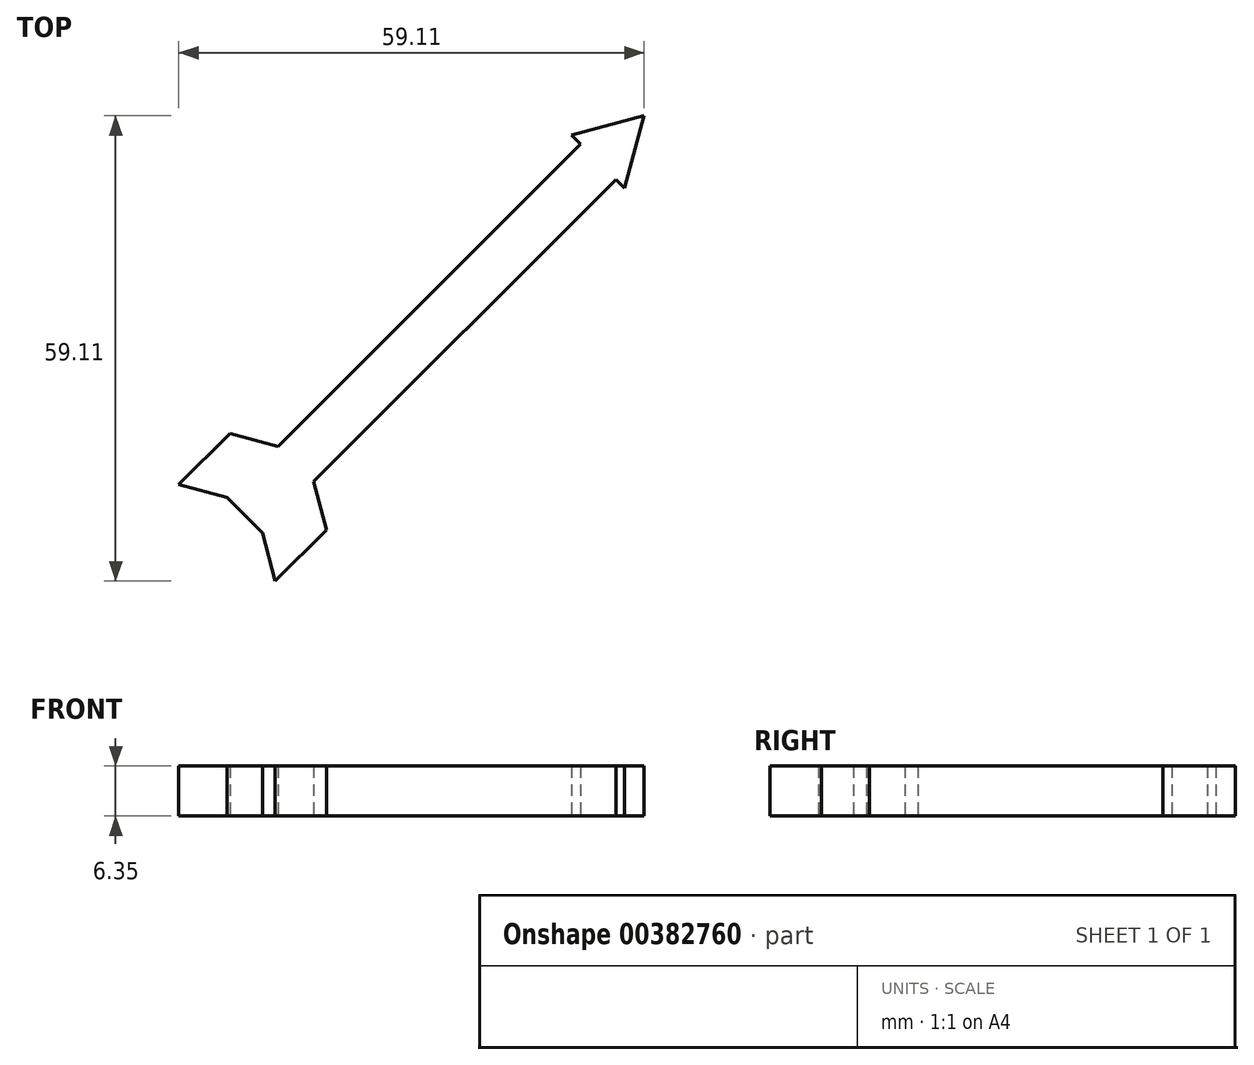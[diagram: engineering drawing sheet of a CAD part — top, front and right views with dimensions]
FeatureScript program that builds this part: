
annotation { "Feature Type Name" : "Feature", "Feature Type Description" : "" }
export const myFeature = defineFeature(function(context is Context, id is Id, definition is map)
    precondition{}
    {
        {
            var Q0;
            Q0=qCreatedBy(makeId("Top.planeOp"),FACE);
            var sketch = newSketch(context, id + "F0", { "sketchPlane" : qUnion([Q0])});
            skArc(sketch, "E0", {"start": v(22.45, -22.45) * mm, "mid": v(22.45, 22.45) * mm, "end": v(-22.45, 22.45) * mm});
            skLineSegment(sketch, "E1", {"start": v(-22.45, 22.45) * mm, "end": v(22.45, -22.45) * mm});
            skArc(sketch, "E2", {"start": v(20.36, -15.57) * mm, "mid": v(20.06, 20.35) * mm, "end": v(-15.86, 20.05) * mm});
            skLineSegment(sketch, "E3", {"start": v(-15.86, 20.05) * mm, "end": v(20.36, -15.57) * mm});
            skLineSegment(sketch, "E4.0", {"start": v(31.43, 35.92) * mm, "end": v(-13.47, -8.98) * mm});
            skLineSegment(sketch, "E5.0", {"start": v(35.92, 31.43) * mm, "end": v(-8.98, -13.47) * mm});
            skLineSegment(sketch, "E6", {"start": v(30.3, 37.04) * mm, "end": v(37.04, 30.3) * mm});
            skLineSegment(sketch, "E7", {"start": v(30.3, 37.04) * mm, "end": v(39.5, 39.5) * mm});
            skLineSegment(sketch, "E8", {"start": v(37.04, 30.3) * mm, "end": v(39.5, 39.5) * mm});
            skPoint(sketch, "E9.start.orphan", {"position": v(22.45, 22.45) * mm});
            skLineSegment(sketch, "E10", {"start": v(-13.47, -8.98) * mm, "end": v(-8.98, -13.47) * mm});
            skLineSegment(sketch, "E11", {"start": v(-6.96, -2.47) * mm, "end": v(-13.1, -0.83) * mm});
            skLineSegment(sketch, "E12", {"start": v(-13.47, -8.98) * mm, "end": v(-19.6, -7.34) * mm});
            skLineSegment(sketch, "E13", {"start": v(-13.1, -0.83) * mm, "end": v(-19.6, -7.34) * mm});
            skLineSegment(sketch, "E14", {"start": v(39.5, 39.5) * mm, "end": v(33.68, 33.68) * mm});
            skLineSegment(sketch, "E15.MirrorCS", {"start": v(-8.98, -13.47) * mm, "end": v(-7.34, -19.6) * mm});
            skLineSegment(sketch, "E16.MirrorCS", {"start": v(-0.83, -13.1) * mm, "end": v(-7.34, -19.6) * mm});
            skLineSegment(sketch, "E17.MirrorCS", {"start": v(-2.47, -6.96) * mm, "end": v(-0.83, -13.1) * mm});
            skSolve(sketch);
        }
        {
            var Q0;
            {var subQ4=sQuery(id+"F0.wireOp",EDGE,"E10");Q0=makeQuery(id+"F0.imprint","IMPRINT",FACE,{"disambiguationData":[TD([[makeQuery(id+"F0.imprint","IMPRINT",EDGE,{"derivedFrom":subQ4}),1.0]])]});}
            var Q1;
            {var subQ2=sQuery(id+"F0.wireOp",EDGE,"E11");Q1=makeQuery(id+"F0.imprint","IMPRINT",FACE,{"disambiguationData":[TD([[makeQuery(id+"F0.imprint","IMPRINT",EDGE,{"derivedFrom":subQ2}),1.0]])]});}
            var Q2;
            {var subQ0=sQuery(id+"F0.wireOp",EDGE,"E15.MirrorCS");Q2=makeQuery(id+"F0.imprint","IMPRINT",FACE,{"disambiguationData":[TD([[makeQuery(id+"F0.imprint","IMPRINT",EDGE,{"derivedFrom":subQ0}),1.0]])]});}
            var Q3;
            {var subQ0=sQuery(id+"F0.wireOp",EDGE,"E4.0");var subQ1=sQuery(id+"F0.wireOp",EDGE,"E1");var subQ2=makeQuery(id+"F0.imprint","INTERSECT",VERTEX,{"derivedFrom":[subQ1,subQ0]});Q3=makeQuery(id+"F0.imprint","IMPRINT",FACE,{"disambiguationData":[TD([[makeQuery(id+"F0.imprint","IMPRINT",EDGE,{"disambiguationData":[TD([[subQ2,-1.0]])],"derivedFrom":subQ1}),1.0]])]});}
            var Q4;
            {var subQ6=sQuery(id+"F0.wireOp",EDGE,"E1");var subQ7=sQuery(id+"F0.wireOp",EDGE,"E0");var subQ8=makeQuery(id+"F0.imprint","INTERSECT",VERTEX,{"disambiguationData":[OD(1.0)],"derivedFrom":[subQ7,subQ6]});Q4=makeQuery(id+"F0.imprint","IMPRINT",FACE,{"disambiguationData":[TD([[makeQuery(id+"F0.imprint","IMPRINT",EDGE,{"disambiguationData":[TD([[subQ8,1.0]])],"derivedFrom":subQ7}),1.0]])]});}
            var Q5;
            {var subQ5=sQuery(id+"F0.wireOp",EDGE,"E1");var subQ6=sQuery(id+"F0.wireOp",EDGE,"E0");var subQ7=makeQuery(id+"F0.imprint","INTERSECT",VERTEX,{"disambiguationData":[OD(0.0)],"derivedFrom":[subQ6,subQ5]});Q5=makeQuery(id+"F0.imprint","IMPRINT",FACE,{"disambiguationData":[TD([[makeQuery(id+"F0.imprint","IMPRINT",EDGE,{"disambiguationData":[TD([[subQ7,-1.0]])],"derivedFrom":subQ6}),1.0]])]});}
            var Q6;
            {var subQ0=sQuery(id+"F0.wireOp",EDGE,"E5.0");var subQ1=sQuery(id+"F0.wireOp",EDGE,"E2");var subQ2=makeQuery(id+"F0.imprint","INTERSECT",VERTEX,{"derivedFrom":[subQ1,subQ0]});Q6=makeQuery(id+"F0.imprint","IMPRINT",FACE,{"disambiguationData":[TD([[makeQuery(id+"F0.imprint","IMPRINT",EDGE,{"disambiguationData":[TD([[subQ2,-1.0]])],"derivedFrom":subQ1}),1.0]])]});}
            var Q7;
            {var subQ4=sQuery(id+"F0.wireOp",EDGE,"E5.0");var subQ6=sQuery(id+"F0.wireOp",EDGE,"E0");var subQ7=makeQuery(id+"F0.imprint","INTERSECT",VERTEX,{"derivedFrom":[subQ6,subQ4]});Q7=makeQuery(id+"F0.imprint","IMPRINT",FACE,{"disambiguationData":[TD([[makeQuery(id+"F0.imprint","IMPRINT",EDGE,{"disambiguationData":[TD([[subQ7,-1.0]])],"derivedFrom":subQ6}),-1.0]])]});}
            var Q8;
            {var subQ0=sQuery(id+"F0.wireOp",EDGE,"E5.0");var subQ1=sQuery(id+"F0.wireOp",EDGE,"E0");var subQ2=makeQuery(id+"F0.imprint","INTERSECT",VERTEX,{"derivedFrom":[subQ1,subQ0]});Q8=makeQuery(id+"F0.imprint","IMPRINT",FACE,{"disambiguationData":[TD([[makeQuery(id+"F0.imprint","IMPRINT",EDGE,{"disambiguationData":[TD([[subQ2,-1.0]])],"derivedFrom":subQ1}),1.0]])]});}
            var Q9;
            {var subQ3=sQuery(id+"F0.wireOp",EDGE,"E8");Q9=makeQuery(id+"F0.imprint","IMPRINT",FACE,{"disambiguationData":[TD([[makeQuery(id+"F0.imprint","IMPRINT",EDGE,{"derivedFrom":subQ3}),1.0]])]});}
            var Q10;
            {var subQ2=sQuery(id+"F0.wireOp",EDGE,"E7");Q10=makeQuery(id+"F0.imprint","IMPRINT",FACE,{"disambiguationData":[TD([[makeQuery(id+"F0.imprint","IMPRINT",EDGE,{"derivedFrom":subQ2}),-1.0]])]});}
            extrude(context, id + "F1", {"entities" : qUnion([Q0, Q1, Q2, Q3, Q4, Q5, Q6, Q7, Q8, Q9, Q10]), "depth" : 6.35 * mm});
        }
    });
